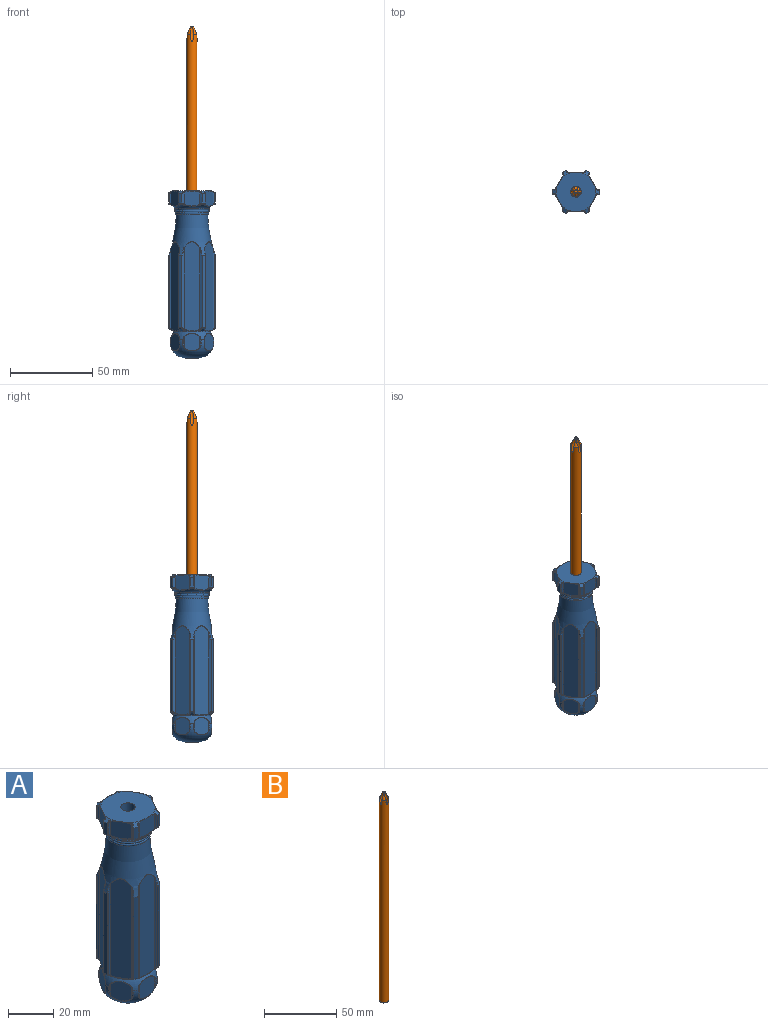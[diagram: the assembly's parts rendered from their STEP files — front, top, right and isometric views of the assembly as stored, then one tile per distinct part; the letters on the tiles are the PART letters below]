
ASSEMBLY  parts=2 mates=1
PART A: 346 faces, bbox 71.6x71.6x105.1 mm
  f0: torus R=10.58mm, axis (0,0,-1), area 19.3mm2, adj f13,f14
  f1: torus R=10mm, axis (0,0,-1), area 2.4mm2, adj f16,f17
  f2: torus R=9.64mm, axis (0,0,-1), area 2.6mm2, adj f19,f20
  f3: cone r=3.17mm half-angle=45deg, axis (0,0,1), area 0.7mm2, adj f4,f35
  f4: cylinder r=3.17mm len=76.17mm, axis (0,0,1), area 1519.6mm2, adj f3,f345
  f5: cone r=12.09mm half-angle=60deg, axis (0,0,-1), area 7.1mm2, adj f35,f306,f307,f308,f309,f310,f337,f338
  f6: cylinder r=0.4mm len=6.09mm, axis (0,0,1), area 4.8mm2, adj f258,f259,f297,f298,f328
  f7: cylinder r=14.29mm len=6.08mm, axis (0,0,1), area 14mm2, adj f256,f294,f295,f323
  f8: cylinder r=0.4mm len=6.41mm, axis (0,0,1), area 5mm2, adj f253,f291,f292,f319
  f9: cylinder r=0.79mm len=7.77mm, axis (0,0,1), area 8.7mm2, adj f234,f235,f305,f335,f336
  f10: cylinder r=0.79mm len=7.77mm, axis (0,0,1), area 8.7mm2, adj f232,f233,f269,f340,f341
  f11: torus R=13.49mm, axis (0,0,-1), area 2.1mm2, adj f12,f230,f237,f267,f268,f308
  f12: torus R=15.87mm, axis (0,0,1), area 169.1mm2, adj f11,f13,f227,f228,f231,f232,f235,f236
  f13: torus R=10.58mm, axis (0,0,1), area 1.6mm2, adj f0,f12
  f14: torus R=9.88mm, axis (0,0,-1), area 74mm2, adj f0,f15
  f15: torus R=10.02mm, axis (0,0,1), area 1.5mm2, adj f14,f16
  f16: torus R=15.87mm, axis (0,0,1), area 2.8mm2, adj f1,f15
  f17: torus R=9.73mm, axis (0,0,-1), area 115.1mm2, adj f1,f18
  f18: torus R=9.64mm, axis (0,0,1), area 2.3mm2, adj f17,f19
  f19: torus R=15.87mm, axis (0,0,1), area 0.8mm2, adj f2,f18
  f20: torus R=9.6mm, axis (0,0,-1), area 127.2mm2, adj f2,f21
  f21: torus R=85.71mm, axis (0,0,1), area 1292.8mm2, adj f20,f22,f203,f204,f205,f206,f207,f208
  f22: torus R=13.49mm, axis (0,0,-1), area 0.6mm2, adj f21,f176,f177,f178,f179,f180
  f23: cylinder r=14.29mm len=43.85mm, axis (0,0,1), area 101.1mm2, adj f155,f156,f157,f225
  f24: cylinder r=0.79mm len=49.79mm, axis (0,0,1), area 58.8mm2, adj f132,f133,f134,f182,f184,f216
  f25: cylinder r=0.79mm len=49.79mm, axis (0,0,1), area 58.8mm2, adj f119,f120,f121,f173,f174,f211
  f26: cylinder r=0.4mm len=43.85mm, axis (0,0,1), area 35mm2, adj f98,f147,f193,f194
  f27: torus R=13.49mm, axis (0,0,-1), area 1.8mm2, adj f29,f93,f94,f124,f129,f179
  f28: cylinder r=0.4mm len=43.85mm, axis (0,0,1), area 35mm2, adj f89,f106,f163,f164
  f29: cone r=11.11mm half-angle=60deg, axis (0,0,1), area 97.3mm2, adj f27,f30,f102,f103,f104,f108,f111,f112
  f30: cylinder r=11.11mm len=22.23mm, axis (0,0,1), area 17.7mm2, adj f29,f31
  f31: torus R=1.9mm, axis (0,0,1), area 189mm2, adj f30,f32,f71,f72,f73,f74,f75,f76
  f32: torus R=3.72mm, axis (0,0,1), area 625.7mm2, adj f31,f50,f51,f52,f53,f54,f55,f56
  f33: cylinder r=0.79mm len=6.25mm, axis (0,0,1), area 2.4mm2, adj f46,f53,f83
  f34: cylinder r=0.79mm len=6.25mm, axis (0,0,1), area 2.4mm2, adj f43,f58,f78
  f35: plane 24.18x23.49mm, normal (0,0,1), area 419.7mm2, adj f3,f5,f319,f323,f324,f328,f329,f333
  f36: cylinder r=0.79mm len=6.25mm, axis (0,0,1), area 11.1mm2, adj f65,f70,f71
  f37: cylinder r=0.79mm len=6.25mm, axis (0,0,1), area 3.3mm2, adj f38,f64,f72
  f38: plane 13.45x11.42mm, normal (0.87,-0.5,0), area 86.3mm2, adj f37,f39,f63,f73
  f39: cylinder r=0.79mm len=6.25mm, axis (0,0,1), area 11.1mm2, adj f38,f62,f74
  f40: cylinder r=0.79mm len=6.25mm, axis (0,0,1), area 3.3mm2, adj f41,f61,f75
  f41: plane 13.45x12.7mm, normal (0,-1,0), area 86.3mm2, adj f40,f42,f60,f76
  f42: cylinder r=0.79mm len=6.25mm, axis (0,0,1), area 11.1mm2, adj f41,f59,f77
  f43: plane 13.45x11.42mm, normal (-0.87,-0.5,0), area 86.3mm2, adj f34,f44,f57,f79
  f44: cylinder r=0.79mm len=6.25mm, axis (0,0,1), area 11.1mm2, adj f43,f56,f80
  f45: cylinder r=0.79mm len=6.25mm, axis (0,0,1), area 3.3mm2, adj f46,f55,f81
  f46: plane 13.45x11.42mm, normal (-0.87,0.5,0), area 86.3mm2, adj f33,f45,f54,f82
  f47: cylinder r=0.79mm len=6.25mm, axis (0,0,1), area 3.3mm2, adj f48,f52,f84
  f48: plane 13.45x12.7mm, normal (0,1,0), area 86.3mm2, adj f47,f49,f51,f85
  f49: cylinder r=0.79mm len=6.25mm, axis (0,0,1), area 11.1mm2, adj f48,f50,f86
  f50: bspline ~4.85x0.92mm, area 1.9mm2, adj f32,f49,f51,f86
  f51: bspline ~9.81x2.14mm, area 2.4mm2, adj f32,f48,f50,f52
  f52: bspline ~4.85x0.92mm, area 1.9mm2, adj f32,f47,f51,f84
  f53: bspline ~4.85x0.9mm, area 1.9mm2, adj f32,f33,f54,f83
  f54: bspline ~8.5x4.91mm, area 2.4mm2, adj f32,f46,f53,f55
  f55: bspline ~4.85x0.68mm, area 1.9mm2, adj f32,f45,f54,f81
  f56: bspline ~4.85x0.68mm, area 1.9mm2, adj f32,f44,f57,f80
  f57: bspline ~8.5x4.91mm, area 2.4mm2, adj f32,f43,f56,f58
  f58: bspline ~4.85x0.9mm, area 1.9mm2, adj f32,f34,f57,f78
  f59: bspline ~4.85x0.92mm, area 1.9mm2, adj f32,f42,f60,f77
  f60: bspline ~9.81x2.14mm, area 2.4mm2, adj f32,f41,f59,f61
  f61: bspline ~4.85x0.92mm, area 1.9mm2, adj f32,f40,f60,f75
  f62: bspline ~4.85x0.91mm, area 1.9mm2, adj f32,f39,f63,f74
  f63: bspline ~8.5x4.91mm, area 2.4mm2, adj f32,f38,f62,f64
  f64: bspline ~4.85x0.68mm, area 1.9mm2, adj f32,f37,f63,f72
  f65: bspline ~4.85x0.68mm, area 1.9mm2, adj f32,f36,f66,f71
  f66: bspline ~8.5x4.91mm, area 2.4mm2, adj f32,f65,f68,f70
  f67: plane 7.44x7.44mm, normal (0,0,-1), area 43.5mm2, adj f32
  f68: bspline ~4.85x0.91mm, area 1.9mm2, adj f32,f66,f69,f87
  f69: cylinder r=0.79mm len=6.25mm, axis (0,0,1), area 3.3mm2, adj f68,f70,f87
  f70: plane 13.45x11.42mm, normal (0.87,0.5,0), area 86.3mm2, adj f36,f66,f69,f88
  f71: bspline ~1.72x0.61mm, area 0.5mm2, adj f31,f36,f65,f88
  f72: bspline ~1.72x0.61mm, area 0.5mm2, adj f31,f37,f64,f73
  f73: bspline ~8.5x4.91mm, area 2.3mm2, adj f31,f38,f72,f74
  f74: bspline ~1.72x0.74mm, area 0.4mm2, adj f31,f39,f62,f73
  f75: bspline ~1.72x0.78mm, area 0.5mm2, adj f31,f40,f61,f76
  f76: bspline ~9.82x2.3mm, area 2.3mm2, adj f31,f41,f75,f77
  f77: bspline ~1.73x0.79mm, area 0.5mm2, adj f31,f42,f59,f76
  f78: bspline ~1.72x0.74mm, area 0.5mm2, adj f31,f34,f58,f79
  f79: bspline ~8.5x4.91mm, area 2.3mm2, adj f31,f43,f78,f80
  f80: bspline ~1.72x0.61mm, area 0.5mm2, adj f31,f44,f56,f79
  f81: bspline ~1.72x0.61mm, area 0.5mm2, adj f31,f45,f55,f82
  f82: bspline ~8.5x4.91mm, area 2.3mm2, adj f31,f46,f81,f83
  f83: bspline ~1.72x0.74mm, area 0.5mm2, adj f31,f33,f53,f82
  f84: bspline ~1.72x0.78mm, area 0.5mm2, adj f31,f47,f52,f85
  f85: bspline ~9.82x2.3mm, area 2.3mm2, adj f31,f48,f84,f86
  f86: bspline ~1.73x0.79mm, area 0.5mm2, adj f31,f49,f50,f85
  f87: bspline ~1.72x0.74mm, area 0.5mm2, adj f31,f68,f69,f88
  f88: bspline ~8.5x4.91mm, area 2.3mm2, adj f31,f70,f71,f87
  f89: bspline ~0.68x0.21mm, area 0.1mm2, adj f28,f105,f106,f108
  f90: bspline ~0.57x0.41mm, area 0.1mm2, adj f107,f108,f109,f110
  f91: bspline ~0.57x0.41mm, area 0.1mm2, adj f114,f115,f117,f118
  f92: bspline ~0.68x0.21mm, area 0.1mm2, adj f116,f118,f119,f120
  f93: bspline ~0.6x0.37mm, area 0.1mm2, adj f27,f124,f125,f127
  f94: bspline ~0.6x0.37mm, area 0.1mm2, adj f27,f126,f128,f129
  f95: bspline ~0.68x0.21mm, area 0.1mm2, adj f133,f134,f136,f137
  f96: bspline ~0.57x0.41mm, area 0.1mm2, adj f135,f137,f138,f139
  f97: bspline ~0.57x0.41mm, area 0.1mm2, adj f143,f144,f145,f146
  f98: bspline ~0.68x0.21mm, area 0.1mm2, adj f26,f146,f147,f148
  f99: bspline ~0.6x0.37mm, area 0.1mm2, adj f101,f153,f155,f157
  f100: bspline ~0.6x0.37mm, area 0.1mm2, adj f152,f154,f156,f157
  f101: bspline ~0.71x0.61mm, area 0.4mm2, adj f99,f102,f157,f158
  f102: bspline ~1.44x1.14mm, area 0.9mm2, adj f29,f101,f103,f158
  f103: bspline ~8.44x4.99mm, area 4.1mm2, adj f29,f102,f104,f159
  f104: bspline ~1.52x1.14mm, area 0.9mm2, adj f29,f103,f105,f160
  f105: bspline ~0.74x0.61mm, area 0.4mm2, adj f89,f104,f108,f160
  f106: plane 44.01x0.01mm, normal (0.5,0.87,0), area 0.4mm2, adj f28,f89,f160,f163
  f107: cylinder r=0.4mm len=43.85mm, axis (0,0,1), area 35mm2, adj f90,f109,f161,f164
  f108: torus R=13.49mm, axis (0,0,-1), area 1.8mm2, adj f29,f89,f90,f105,f110,f164
  f109: plane 44.01x0.01mm, normal (-1,0,0), area 0.4mm2, adj f90,f107,f161,f166
  f110: bspline ~0.61x0.58mm, area 0.4mm2, adj f90,f108,f111,f166
  f111: bspline ~1.26x1.14mm, area 0.9mm2, adj f29,f110,f112,f166
  f112: bspline ~9.68x0.9mm, area 4.1mm2, adj f29,f111,f113,f167
  f113: bspline ~1.26x1.14mm, area 0.9mm2, adj f29,f112,f114,f168
  f114: bspline ~0.61x0.58mm, area 0.4mm2, adj f91,f113,f118,f168
  f115: plane 44.01x0.01mm, normal (1,0,0), area 0.4mm2, adj f91,f117,f168,f171
  f116: cylinder r=0.4mm len=43.85mm, axis (0,0,1), area 35mm2, adj f92,f119,f169,f172
  f117: cylinder r=0.4mm len=43.85mm, axis (0,0,1), area 35mm2, adj f91,f115,f171,f172
  f118: torus R=13.49mm, axis (0,0,-1), area 1.8mm2, adj f29,f91,f92,f114,f120,f172
  f119: plane 44.01x0.01mm, normal (-0.5,0.87,0), area 0.4mm2, adj f25,f92,f116,f169
  f120: bspline ~0.74x0.61mm, area 0.4mm2, adj f25,f92,f118,f121
  f121: bspline ~1.52x1.14mm, area 0.9mm2, adj f25,f29,f120,f122
  f122: bspline ~8.44x4.99mm, area 4.1mm2, adj f29,f121,f123,f174
  f123: bspline ~1.44x1.14mm, area 0.9mm2, adj f29,f122,f124,f175
  f124: bspline ~0.71x0.61mm, area 0.4mm2, adj f27,f93,f123,f175
  f125: plane 44.01x0.01mm, normal (0.5,-0.87,0), area 0.4mm2, adj f93,f127,f175,f178
  f126: cylinder r=0.4mm len=43.85mm, axis (0,0,1), area 35mm2, adj f94,f128,f176,f179
  f127: cylinder r=0.4mm len=43.85mm, axis (0,0,1), area 35mm2, adj f93,f125,f178,f179
  f128: plane 44.01x0.01mm, normal (0.5,0.87,0), area 0.4mm2, adj f94,f126,f176,f181
  f129: bspline ~0.71x0.61mm, area 0.4mm2, adj f27,f94,f130,f181
  f130: bspline ~1.44x1.14mm, area 0.9mm2, adj f29,f129,f131,f181
  f131: bspline ~8.44x4.99mm, area 4.1mm2, adj f29,f130,f132,f182
  f132: bspline ~1.52x1.14mm, area 0.9mm2, adj f24,f29,f131,f133
  f133: bspline ~0.74x0.61mm, area 0.4mm2, adj f24,f95,f132,f137
  f134: plane 44.01x0.01mm, normal (-0.5,-0.87,0), area 0.4mm2, adj f24,f95,f136,f185
  f135: cylinder r=0.4mm len=43.85mm, axis (0,0,1), area 35mm2, adj f96,f138,f183,f186
  f136: cylinder r=0.4mm len=43.85mm, axis (0,0,1), area 35mm2, adj f95,f134,f185,f186
  f137: torus R=13.49mm, axis (0,0,-1), area 1.8mm2, adj f29,f95,f96,f133,f139,f186
  f138: plane 44.01x0.01mm, normal (1,0,0), area 0.4mm2, adj f96,f135,f183,f188
  f139: bspline ~0.61x0.58mm, area 0.4mm2, adj f96,f137,f140,f188
  f140: bspline ~1.26x1.14mm, area 0.9mm2, adj f29,f139,f141,f188
  f141: bspline ~9.68x0.9mm, area 4.1mm2, adj f29,f140,f142,f189
  f142: bspline ~1.26x1.14mm, area 0.9mm2, adj f29,f141,f143,f190
  f143: bspline ~0.61x0.58mm, area 0.4mm2, adj f97,f142,f146,f190
  f144: plane 44.01x0.01mm, normal (-1,0,0), area 0.4mm2, adj f97,f145,f190,f192
  f145: cylinder r=0.4mm len=43.85mm, axis (0,0,1), area 35mm2, adj f97,f144,f192,f193
  f146: torus R=13.49mm, axis (0,0,-1), area 1.8mm2, adj f29,f97,f98,f143,f148,f193
  f147: plane 44.01x0.01mm, normal (0.5,-0.87,0), area 0.4mm2, adj f26,f98,f194,f196
  f148: bspline ~0.74x0.61mm, area 0.4mm2, adj f98,f146,f149,f196
  f149: bspline ~1.52x1.14mm, area 0.9mm2, adj f29,f148,f150,f196
  f150: bspline ~8.44x4.99mm, area 4.1mm2, adj f29,f149,f151,f197
  f151: bspline ~1.44x1.14mm, area 0.9mm2, adj f29,f150,f152,f198
  f152: bspline ~0.71x0.61mm, area 0.4mm2, adj f100,f151,f157,f198
  f153: plane 44.01x0.01mm, normal (-0.5,-0.87,0), area 0.4mm2, adj f99,f155,f158,f199
  f154: plane 44.01x0.01mm, normal (-0.5,0.87,0), area 0.4mm2, adj f100,f156,f198,f202
  f155: cylinder r=0.4mm len=43.85mm, axis (0,0,1), area 35mm2, adj f23,f99,f153,f199
  f156: cylinder r=0.4mm len=43.85mm, axis (0,0,1), area 35mm2, adj f23,f100,f154,f202
  f157: torus R=13.49mm, axis (0,0,-1), area 1.8mm2, adj f23,f29,f99,f100,f101,f152
  f158: cylinder r=0.79mm len=49.79mm, axis (0,0,1), area 58.8mm2, adj f101,f102,f153,f159,f200,f203
  f159: plane 53.86x8.25mm, normal (0.87,-0.5,0), area 499.5mm2, adj f103,f158,f160,f204
  f160: cylinder r=0.79mm len=49.79mm, axis (0,0,1), area 58.8mm2, adj f104,f105,f106,f159,f162,f205
  f161: bspline ~0.57x0.41mm, area 0.1mm2, adj f107,f109,f165,f206
  f162: bspline ~0.67x0.21mm, area 0.1mm2, adj f160,f163,f205,f206
  f163: bspline ~0.68x0.21mm, area 0.1mm2, adj f28,f106,f162,f206
  f164: cylinder r=14.29mm len=43.85mm, axis (0,0,1), area 101.1mm2, adj f28,f107,f108,f206
  f165: bspline ~0.56x0.4mm, area 0.1mm2, adj f161,f166,f206,f207
  f166: cylinder r=0.79mm len=49.79mm, axis (0,0,1), area 58.8mm2, adj f109,f110,f111,f165,f167,f207
  f167: plane 53.86x9.53mm, normal (0,-1,0), area 499.5mm2, adj f112,f166,f168,f208
  f168: cylinder r=0.79mm len=49.79mm, axis (0,0,1), area 58.8mm2, adj f113,f114,f115,f167,f170,f209
  f169: bspline ~0.68x0.21mm, area 0.1mm2, adj f116,f119,f173,f210
  f170: bspline ~0.56x0.4mm, area 0.1mm2, adj f168,f171,f209,f210
  f171: bspline ~0.57x0.41mm, area 0.1mm2, adj f115,f117,f170,f210
  f172: cylinder r=14.29mm len=43.85mm, axis (0,0,1), area 101.1mm2, adj f116,f117,f118,f210
  f173: bspline ~0.67x0.21mm, area 0.1mm2, adj f25,f169,f210,f211
  f174: plane 53.86x8.25mm, normal (-0.87,-0.5,0), area 499.5mm2, adj f25,f122,f175,f212
  f175: cylinder r=0.79mm len=49.79mm, axis (0,0,1), area 58.8mm2, adj f123,f124,f125,f174,f177,f213
  f176: bspline ~0.6x0.37mm, area 0.1mm2, adj f22,f126,f128,f180
  f177: bspline ~0.6x0.37mm, area 0.1mm2, adj f22,f175,f178,f213
  f178: bspline ~0.6x0.37mm, area 0.1mm2, adj f22,f125,f127,f177
  f179: cylinder r=14.29mm len=43.85mm, axis (0,0,1), area 101.1mm2, adj f22,f27,f126,f127
  f180: bspline ~0.6x0.37mm, area 0.1mm2, adj f22,f176,f181,f214
  f181: cylinder r=0.79mm len=49.79mm, axis (0,0,1), area 58.8mm2, adj f128,f129,f130,f180,f182,f214
  f182: plane 53.86x8.25mm, normal (-0.87,0.5,0), area 499.4mm2, adj f24,f131,f181,f215
  f183: bspline ~0.57x0.41mm, area 0.1mm2, adj f135,f138,f187,f217
  f184: bspline ~0.67x0.21mm, area 0.1mm2, adj f24,f185,f216,f217
  f185: bspline ~0.68x0.21mm, area 0.1mm2, adj f134,f136,f184,f217
  f186: cylinder r=14.29mm len=43.85mm, axis (0,0,1), area 101.1mm2, adj f135,f136,f137,f217
  f187: bspline ~0.56x0.4mm, area 0.1mm2, adj f183,f188,f217,f218
  f188: cylinder r=0.79mm len=49.79mm, axis (0,0,1), area 58.8mm2, adj f138,f139,f140,f187,f189,f218
  f189: plane 53.86x9.53mm, normal (0,1,0), area 499.5mm2, adj f141,f188,f190,f219
  f190: cylinder r=0.79mm len=49.79mm, axis (0,0,1), area 58.8mm2, adj f142,f143,f144,f189,f191,f220
  f191: bspline ~0.56x0.4mm, area 0.1mm2, adj f190,f192,f220,f221
  f192: bspline ~0.57x0.41mm, area 0.1mm2, adj f144,f145,f191,f221
  f193: cylinder r=14.29mm len=43.85mm, axis (0,0,1), area 101.1mm2, adj f26,f145,f146,f221
  f194: bspline ~0.68x0.21mm, area 0.1mm2, adj f26,f147,f195,f221
  f195: bspline ~0.67x0.21mm, area 0.1mm2, adj f194,f196,f221,f222
  f196: cylinder r=0.79mm len=49.79mm, axis (0,0,1), area 58.8mm2, adj f147,f148,f149,f195,f197,f222
  f197: plane 53.86x8.25mm, normal (0.87,0.5,0), area 499.5mm2, adj f150,f196,f198,f223
  f198: cylinder r=0.79mm len=49.79mm, axis (0,0,1), area 58.8mm2, adj f151,f152,f154,f197,f201,f224
  f199: bspline ~0.6x0.37mm, area 0.1mm2, adj f153,f155,f200,f225
  f200: bspline ~0.6x0.37mm, area 0.1mm2, adj f158,f199,f203,f225
  f201: bspline ~0.6x0.37mm, area 0.1mm2, adj f198,f202,f224,f225
  f202: bspline ~0.6x0.37mm, area 0.1mm2, adj f154,f156,f201,f225
  f203: bspline ~4.78x1.64mm, area 2.5mm2, adj f21,f158,f200,f204
  f204: bspline ~8.5x4.91mm, area 1.7mm2, adj f21,f159,f203,f205
  f205: bspline ~4.78x1.73mm, area 2.5mm2, adj f21,f160,f162,f204
  f206: torus R=13.49mm, axis (0,0,-1), area 0.6mm2, adj f21,f161,f162,f163,f164,f165
  f207: bspline ~4.78x1.35mm, area 2.5mm2, adj f21,f165,f166,f208
  f208: bspline ~9.82x3.61mm, area 1.7mm2, adj f21,f167,f207,f209
  f209: bspline ~4.78x1.35mm, area 2.5mm2, adj f21,f168,f170,f208
  f210: torus R=13.49mm, axis (0,0,-1), area 0.6mm2, adj f21,f169,f170,f171,f172,f173
  f211: bspline ~4.78x1.73mm, area 2.5mm2, adj f21,f25,f173,f212
  f212: bspline ~8.5x4.91mm, area 1.7mm2, adj f21,f174,f211,f213
  f213: bspline ~4.78x1.64mm, area 2.5mm2, adj f21,f175,f177,f212
  f214: bspline ~4.78x1.64mm, area 2.5mm2, adj f21,f180,f181,f215
  f215: bspline ~8.5x4.91mm, area 1.7mm2, adj f21,f182,f214,f216
  f216: bspline ~4.78x1.73mm, area 2.5mm2, adj f21,f24,f184,f215
  f217: torus R=13.49mm, axis (0,0,-1), area 0.6mm2, adj f21,f183,f184,f185,f186,f187
  f218: bspline ~4.78x1.35mm, area 2.5mm2, adj f21,f187,f188,f219
  f219: bspline ~9.82x3.61mm, area 1.7mm2, adj f21,f189,f218,f220
  f220: bspline ~4.78x1.35mm, area 2.5mm2, adj f21,f190,f191,f219
  f221: torus R=13.49mm, axis (0,0,-1), area 0.6mm2, adj f21,f191,f192,f193,f194,f195
  f222: bspline ~4.78x1.73mm, area 2.5mm2, adj f21,f195,f196,f223
  f223: bspline ~8.5x4.91mm, area 1.7mm2, adj f21,f197,f222,f224
  f224: bspline ~4.78x1.64mm, area 2.5mm2, adj f21,f198,f201,f223
  f225: torus R=13.49mm, axis (0,0,-1), area 0.6mm2, adj f21,f23,f199,f200,f201,f202
  f226: bspline ~0.67x0.58mm, area 0.5mm2, adj f227,f271,f272,f274
  f227: bspline ~1.22x0.97mm, area 0.7mm2, adj f12,f226,f273,f274
  f228: bspline ~1.22x0.97mm, area 0.7mm2, adj f12,f229,f273,f275
  f229: bspline ~0.67x0.58mm, area 0.5mm2, adj f228,f251,f252,f275
  f230: bspline ~0.75x0.67mm, area 0.5mm2, adj f11,f231,f268,f277
  f231: bspline ~1.3x0.97mm, area 0.7mm2, adj f12,f230,f276,f277
  f232: bspline ~1.41x0.97mm, area 0.7mm2, adj f10,f12,f233,f276
  f233: bspline ~0.77x0.67mm, area 0.5mm2, adj f10,f232,f270,f271
  f234: bspline ~0.77x0.67mm, area 0.5mm2, adj f9,f235,f264,f265
  f235: bspline ~1.41x0.97mm, area 0.7mm2, adj f9,f12,f234,f278
  f236: bspline ~1.3x0.97mm, area 0.7mm2, adj f12,f237,f278,f279
  f237: bspline ~0.75x0.67mm, area 0.5mm2, adj f11,f236,f267,f279
  f238: bspline ~0.67x0.58mm, area 0.5mm2, adj f239,f260,f261,f281
  f239: bspline ~1.22x0.97mm, area 0.7mm2, adj f12,f238,f280,f281
  f240: bspline ~1.22x0.97mm, area 0.7mm2, adj f12,f241,f280,f282
  f241: bspline ~0.67x0.58mm, area 0.5mm2, adj f240,f263,f264,f282
  f242: bspline ~0.75x0.67mm, area 0.5mm2, adj f243,f256,f257,f284
  f243: bspline ~1.3x0.97mm, area 0.7mm2, adj f12,f242,f283,f284
  f244: bspline ~1.41x0.97mm, area 0.7mm2, adj f12,f245,f283,f285
  f245: bspline ~0.77x0.67mm, area 0.5mm2, adj f244,f259,f260,f285
  f246: bspline ~0.77x0.67mm, area 0.5mm2, adj f247,f252,f253,f287
  f247: bspline ~1.41x0.97mm, area 0.7mm2, adj f12,f246,f286,f287
  f248: bspline ~1.3x0.97mm, area 0.7mm2, adj f12,f249,f286,f288
  f249: bspline ~0.75x0.67mm, area 0.5mm2, adj f248,f255,f256,f288
  f250: plane 5.94x0.01mm, normal (-1,0,0), area 0.1mm2, adj f251,f275,f289,f290
  f251: bspline ~0.57x0.41mm, area 0.1mm2, adj f229,f250,f252,f290
  f252: torus R=13.49mm, axis (0,0,-1), area 2.1mm2, adj f12,f229,f246,f251,f253,f291
  f253: bspline ~0.68x0.21mm, area 0.1mm2, adj f8,f246,f252,f292
  f254: plane 5.94x0.01mm, normal (-0.5,0.87,0), area 0.1mm2, adj f255,f288,f293,f294
  f255: bspline ~0.6x0.37mm, area 0.1mm2, adj f249,f254,f256,f294
  f256: torus R=13.49mm, axis (0,0,-1), area 2.1mm2, adj f7,f12,f242,f249,f255,f257
  f257: bspline ~0.6x0.37mm, area 0.1mm2, adj f242,f256,f295,f296
  f258: plane 5.94x0.01mm, normal (0.5,0.87,0), area 0.1mm2, adj f6,f259,f285,f297
  f259: bspline ~0.68x0.21mm, area 0.1mm2, adj f6,f245,f258,f260
  f260: torus R=13.49mm, axis (0,0,-1), area 2.1mm2, adj f12,f238,f245,f259,f261,f298
  f261: bspline ~0.57x0.41mm, area 0.1mm2, adj f238,f260,f299,f300
  f262: plane 5.94x0.01mm, normal (1,0,0), area 0.1mm2, adj f263,f282,f301,f302
  f263: bspline ~0.57x0.41mm, area 0.1mm2, adj f241,f262,f264,f302
  f264: torus R=13.49mm, axis (0,0,-1), area 2.1mm2, adj f12,f234,f241,f263,f265,f303
  f265: bspline ~0.68x0.21mm, area 0.1mm2, adj f234,f264,f304,f305
  f266: plane 5.94x0.01mm, normal (0.5,-0.87,0), area 0.1mm2, adj f267,f279,f306,f307
  f267: bspline ~0.6x0.37mm, area 0.1mm2, adj f11,f237,f266,f307
  f268: bspline ~0.6x0.37mm, area 0.1mm2, adj f11,f230,f309,f310
  f269: plane 5.94x0.01mm, normal (-0.5,-0.87,0), area 0.1mm2, adj f10,f270,f311,f312
  f270: bspline ~0.68x0.21mm, area 0.1mm2, adj f233,f269,f271,f312
  f271: torus R=13.49mm, axis (0,0,-1), area 2.1mm2, adj f12,f226,f233,f270,f272,f313
  f272: bspline ~0.57x0.41mm, area 0.1mm2, adj f226,f271,f314,f315
  f273: bspline ~9.69x1.02mm, area 3.5mm2, adj f12,f227,f228,f317
  f274: cylinder r=0.79mm len=7.77mm, axis (0,0,1), area 8.6mm2, adj f226,f227,f315,f316,f317
  f275: cylinder r=0.79mm len=7.77mm, axis (0,0,1), area 8.6mm2, adj f228,f229,f250,f317,f318
  f276: bspline ~8.44x4.99mm, area 3.5mm2, adj f12,f231,f232,f340
  f277: cylinder r=0.79mm len=7.77mm, axis (0,0,1), area 8.6mm2, adj f230,f231,f310,f339,f340
  f278: bspline ~8.44x4.99mm, area 3.5mm2, adj f12,f235,f236,f336
  f279: cylinder r=0.79mm len=7.77mm, axis (0,0,1), area 8.6mm2, adj f236,f237,f266,f336,f337
  f280: bspline ~9.69x1.02mm, area 3.5mm2, adj f12,f239,f240,f331
  f281: cylinder r=0.79mm len=7.77mm, axis (0,0,1), area 8.6mm2, adj f238,f239,f300,f330,f331
  f282: cylinder r=0.79mm len=7.77mm, axis (0,0,1), area 8.6mm2, adj f240,f241,f262,f331,f332
  f283: bspline ~8.44x4.99mm, area 3.5mm2, adj f12,f243,f244,f326
  f284: cylinder r=0.79mm len=7.77mm, axis (0,0,1), area 8.6mm2, adj f242,f243,f296,f325,f326
  f285: cylinder r=0.79mm len=7.77mm, axis (0,0,1), area 8.6mm2, adj f244,f245,f258,f326,f327
  f286: bspline ~8.44x4.99mm, area 3.5mm2, adj f12,f247,f248,f321
  f287: cylinder r=0.79mm len=7.77mm, axis (0,0,1), area 8.6mm2, adj f246,f247,f292,f320,f321
  f288: cylinder r=0.79mm len=7.77mm, axis (0,0,1), area 8.6mm2, adj f248,f249,f254,f321,f322
  f289: bspline ~0.48x0.47mm, area 0.1mm2, adj f250,f290,f318,f319
  f290: cylinder r=0.4mm len=6.09mm, axis (0,0,1), area 4.8mm2, adj f250,f251,f289,f291,f319
  f291: cylinder r=14.29mm len=6.08mm, axis (0,0,1), area 14mm2, adj f8,f252,f290,f319
  f292: plane 7.11x0.89mm, normal (0.5,-0.87,0), area 0.2mm2, adj f8,f253,f287,f319,f320
  f293: bspline ~0.59x0.48mm, area 0.1mm2, adj f254,f294,f322,f323
  f294: cylinder r=0.4mm len=6.09mm, axis (0,0,1), area 4.8mm2, adj f7,f254,f255,f293,f323
  f295: cylinder r=0.4mm len=6.41mm, axis (0,0,1), area 5mm2, adj f7,f257,f296,f323
  f296: plane 7.11x0.89mm, normal (-0.5,-0.87,0), area 0.2mm2, adj f257,f284,f295,f323,f325
  f297: bspline ~0.62x0.48mm, area 0.1mm2, adj f6,f258,f327,f328
  f298: cylinder r=14.29mm len=6.08mm, axis (0,0,1), area 14mm2, adj f6,f260,f299,f328
  f299: cylinder r=0.4mm len=6.41mm, axis (0,0,1), area 5mm2, adj f261,f298,f300,f328
  f300: plane 7.11x1mm, normal (-1,0,0), area 0.2mm2, adj f261,f281,f299,f328,f330
  f301: bspline ~0.48x0.48mm, area 0.1mm2, adj f262,f302,f332,f333
  f302: cylinder r=0.4mm len=6.09mm, axis (0,0,1), area 4.8mm2, adj f262,f263,f301,f303,f333
  f303: cylinder r=14.29mm len=6.08mm, axis (0,0,1), area 14mm2, adj f264,f302,f304,f333
  f304: cylinder r=0.4mm len=6.41mm, axis (0,0,1), area 5mm2, adj f265,f303,f305,f333
  f305: plane 7.11x0.89mm, normal (-0.5,0.87,0), area 0.2mm2, adj f9,f265,f304,f333,f335
  f306: bspline ~0.59x0.48mm, area 0.1mm2, adj f5,f266,f307,f337
  f307: cylinder r=0.4mm len=6.09mm, axis (0,0,1), area 4.8mm2, adj f5,f266,f267,f306,f308
  f308: cylinder r=14.29mm len=6.08mm, axis (0,0,1), area 14mm2, adj f5,f11,f307,f309
  f309: cylinder r=0.4mm len=6.41mm, axis (0,0,1), area 5mm2, adj f5,f268,f308,f310
  f310: plane 7.11x0.89mm, normal (0.5,0.87,0), area 0.2mm2, adj f5,f268,f277,f309,f339
  f311: bspline ~0.62x0.48mm, area 0.1mm2, adj f269,f312,f341,f342
  f312: cylinder r=0.4mm len=6.09mm, axis (0,0,1), area 4.8mm2, adj f269,f270,f311,f313,f342
  f313: cylinder r=14.29mm len=6.08mm, axis (0,0,1), area 14mm2, adj f271,f312,f314,f342
  f314: cylinder r=0.4mm len=6.41mm, axis (0,0,1), area 5mm2, adj f272,f313,f315,f342
  f315: plane 7.11x1mm, normal (1,0,0), area 0.2mm2, adj f272,f274,f314,f316,f342
  f316: bspline ~1.28x1.26mm, area 0.6mm2, adj f274,f315,f342,f344
  f317: plane 9.56x9.08mm, normal (0,1,0), area 81.9mm2, adj f273,f274,f275,f344
  f318: bspline ~1.28x1.25mm, area 1mm2, adj f275,f289,f319,f344
  f319: cone r=12.09mm half-angle=60deg, axis (0,0,-1), area 7.1mm2, adj f8,f35,f289,f290,f291,f292,f318,f320
  f320: bspline ~1.64x1.26mm, area 0.6mm2, adj f287,f292,f319,f324
  f321: plane 9.08x8.28mm, normal (0.87,0.5,0), area 81.9mm2, adj f286,f287,f288,f324
  f322: bspline ~1.63x1.25mm, area 1mm2, adj f288,f293,f323,f324
  f323: cone r=12.09mm half-angle=60deg, axis (0,0,-1), area 7.1mm2, adj f7,f35,f293,f294,f295,f296,f322,f324
  f324: bspline ~8.44x4.99mm, area 2.1mm2, adj f35,f319,f320,f321,f322,f323
  f325: bspline ~1.64x1.26mm, area 0.6mm2, adj f284,f296,f323,f329
  f326: plane 9.08x8.28mm, normal (0.87,-0.5,0), area 81.9mm2, adj f283,f284,f285,f329
  f327: bspline ~1.63x1.25mm, area 1mm2, adj f285,f297,f328,f329
  f328: cone r=12.09mm half-angle=60deg, axis (0,0,-1), area 7.1mm2, adj f6,f35,f297,f298,f299,f300,f327,f329
  f329: bspline ~8.44x4.99mm, area 2.1mm2, adj f35,f323,f325,f326,f327,f328
  f330: bspline ~1.28x1.26mm, area 0.6mm2, adj f281,f300,f328,f334
  f331: plane 9.56x9.08mm, normal (0,-1,0), area 81.9mm2, adj f280,f281,f282,f334
  f332: bspline ~1.28x1.25mm, area 1mm2, adj f282,f301,f333,f334
  f333: cone r=12.09mm half-angle=60deg, axis (0,0,-1), area 7.1mm2, adj f35,f301,f302,f303,f304,f305,f332,f334
  f334: bspline ~9.68x0.9mm, area 2.1mm2, adj f35,f328,f330,f331,f332,f333
  f335: bspline ~1.64x1.26mm, area 0.6mm2, adj f9,f305,f333,f338
  f336: plane 9.08x8.28mm, normal (-0.87,-0.5,0), area 81.9mm2, adj f9,f278,f279,f338
  f337: bspline ~1.63x1.25mm, area 1mm2, adj f5,f279,f306,f338
  f338: bspline ~8.44x4.99mm, area 2.1mm2, adj f5,f35,f333,f335,f336,f337
  f339: bspline ~1.64x1.26mm, area 0.6mm2, adj f5,f277,f310,f343
  f340: plane 9.08x8.28mm, normal (-0.87,0.5,0), area 81.9mm2, adj f10,f276,f277,f343
  f341: bspline ~1.63x1.25mm, area 1mm2, adj f10,f311,f342,f343
  f342: cone r=12.09mm half-angle=60deg, axis (0,0,-1), area 7.1mm2, adj f35,f311,f312,f313,f314,f315,f316,f341
  f343: bspline ~8.44x4.99mm, area 2.1mm2, adj f5,f35,f339,f340,f341,f342
  f344: bspline ~9.68x0.9mm, area 2.1mm2, adj f35,f316,f317,f318,f319,f342
  f345: plane 6.35x6.35mm, normal (0,0,1), area 31.7mm2, adj f4
PART B: 12 faces, bbox 7.4x7.4x176.5 mm
  f0: revolved ~9.12x2.85mm, area 27.7mm2, adj f4,f5,f6,f7
  f1: revolved ~9.12x2.85mm, area 27.7mm2, adj f4,f5,f7,f8
  f2: revolved ~9.12x2.85mm, area 27.7mm2, adj f4,f5,f8,f9
  f3: revolved ~9.12x2.85mm, area 27.7mm2, adj f4,f5,f6,f9
  f4: cone r=3.17mm half-angle=25.1deg, axis (0,0,-1), area 34.4mm2, adj f0,f1,f2,f3,f6,f7,f8,f9
  f5: cylinder r=3.17mm len=171.27mm, axis (0,0,1), area 3389.3mm2, adj f0,f1,f2,f3,f6,f7,f8,f9
  f6: torus R=2.38mm, axis (0,0,-1), area 1mm2, adj f0,f3,f4,f5
  f7: torus R=2.38mm, axis (0,0,-1), area 1mm2, adj f0,f1,f4,f5
  f8: torus R=2.38mm, axis (0,0,-1), area 1mm2, adj f1,f2,f4,f5
  f9: torus R=2.38mm, axis (0,0,-1), area 1mm2, adj f2,f3,f4,f5
  f10: plane 1.59x1.59mm, normal (0,0,1), area 2mm2, adj f4
  f11: plane 6.35x6.35mm, normal (0,0,-1), area 31.7mm2, adj f5
PLACE A at identity
PLACE B at identity fixed
MATE fastened B.f4 <-> A.f0  axis (0,0,-1) through (0,0,25.4)mm
